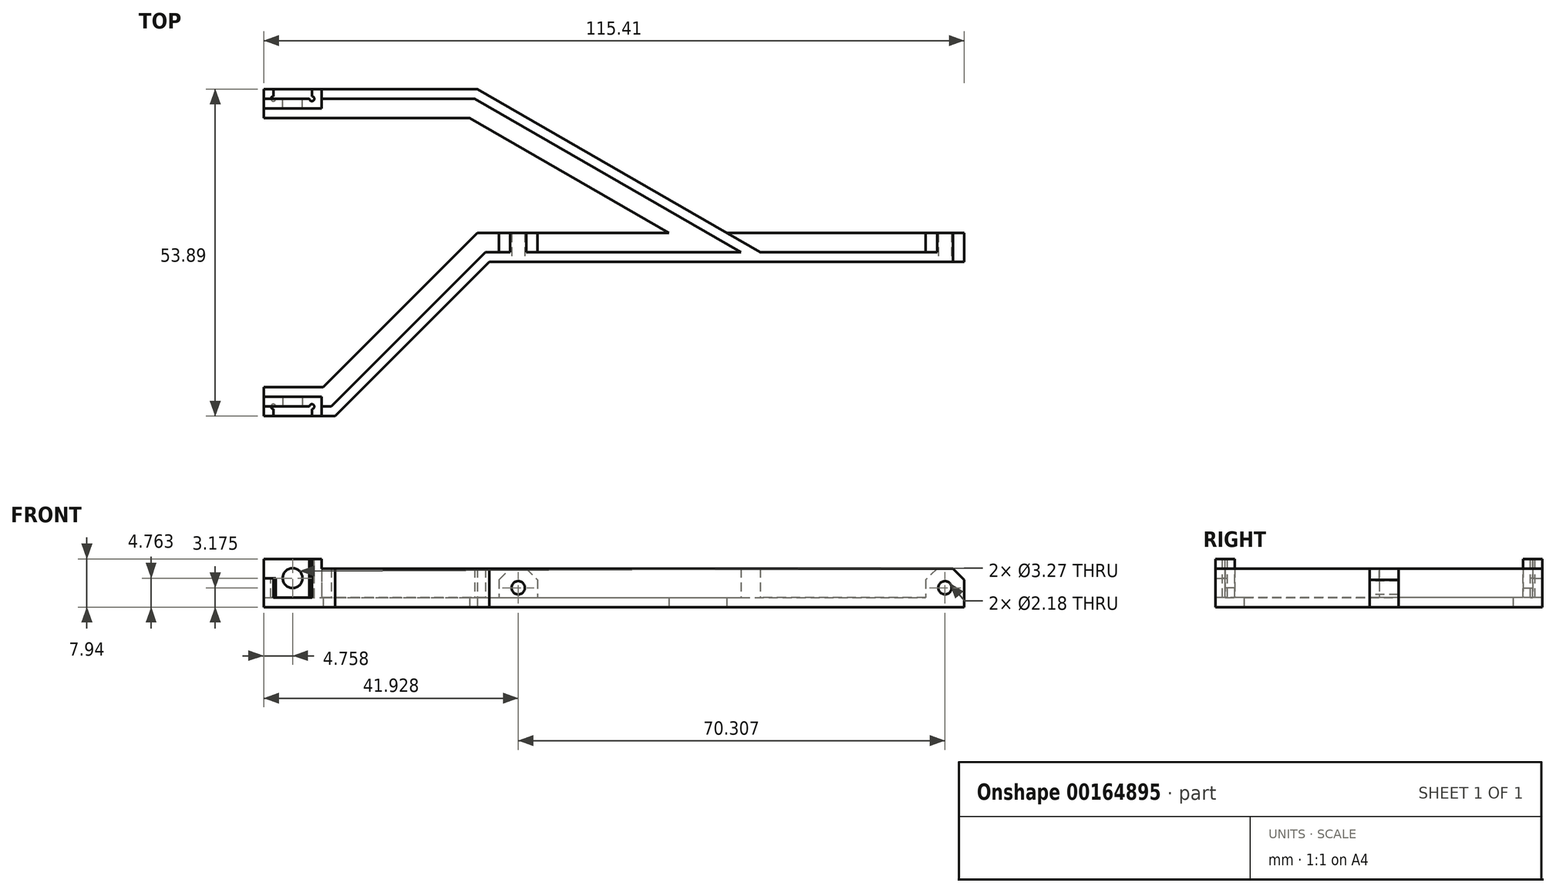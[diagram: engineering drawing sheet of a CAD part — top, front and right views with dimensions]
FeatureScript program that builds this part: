
annotation { "Feature Type Name" : "Feature", "Feature Type Description" : "" }
export const myFeature = defineFeature(function(context is Context, id is Id, definition is map)
    precondition{}
    {
        {
            var Q0;
            Q0=qCreatedBy(makeId("Top.planeOp"),FACE);
            var sketch = newSketch(context, id + "F0", { "sketchPlane" : qUnion([Q0])});
            skLineSegment(sketch, "E0", {"start": v(-127, 25.4) * mm, "end": v(-87.88, 25.4) * mm});
            skLineSegment(sketch, "E1", {"start": v(-46.78, 25.4) * mm, "end": v(-21.38, 0) * mm});
            skLineSegment(sketch, "E2", {"start": v(-21.38, 0) * mm, "end": v(21.38, 0) * mm});
            skLineSegment(sketch, "E3", {"start": v(21.38, 0) * mm, "end": v(46.78, 25.4) * mm});
            skLineSegment(sketch, "E4", {"start": v(87.88, 25.4) * mm, "end": v(127, 25.4) * mm});
            skLineSegment(sketch, "E5", {"start": v(-127, 25.4) * mm, "end": v(-127, 20.64) * mm});
            skLineSegment(sketch, "E6", {"start": v(-127, 20.64) * mm, "end": v(-48.76, 20.64) * mm});
            skLineSegment(sketch, "E7", {"start": v(-48.76, 20.64) * mm, "end": v(-23.36, -4.76) * mm});
            skLineSegment(sketch, "E8", {"start": v(-23.36, -4.76) * mm, "end": v(23.36, -4.76) * mm});
            skLineSegment(sketch, "E9", {"start": v(23.36, -4.76) * mm, "end": v(48.76, 20.64) * mm});
            skLineSegment(sketch, "E10", {"start": v(48.76, 20.64) * mm, "end": v(127, 20.64) * mm});
            skLineSegment(sketch, "E11", {"start": v(127, 20.64) * mm, "end": v(127, 25.4) * mm});
            skLineSegment(sketch, "E12", {"start": v(-34.08, 12.7) * mm, "end": v(-37.45, 9.33) * mm, "construction": true});
            skLineSegment(sketch, "E13", {"start": v(0, 0) * mm, "end": v(0, -4.76) * mm, "construction": true});
            skLineSegment(sketch, "E14", {"start": v(34.08, 12.7) * mm, "end": v(37.45, 9.33) * mm, "construction": true});
            skLineSegment(sketch, "E15", {"start": v(-87.88, 20.64) * mm, "end": v(-87.88, 25.4) * mm, "construction": true});
            skLineSegment(sketch, "E16", {"start": v(87.88, 20.64) * mm, "end": v(87.88, 25.4) * mm, "construction": true});
            skLineSegment(sketch, "E17", {"start": v(-87.88, 25.4) * mm, "end": v(-46.78, 49.13) * mm});
            skLineSegment(sketch, "E18", {"start": v(-78.35, 25.4) * mm, "end": v(-45.5, 44.36) * mm});
            skLineSegment(sketch, "E19", {"start": v(-45.5, 44.36) * mm, "end": v(45.5, 44.36) * mm});
            skLineSegment(sketch, "E20", {"start": v(-46.78, 49.13) * mm, "end": v(46.78, 49.13) * mm});
            skLineSegment(sketch, "E21", {"start": v(-78.35, 25.4) * mm, "end": v(-46.78, 25.4) * mm});
            skLineSegment(sketch, "E22", {"start": v(45.5, 44.36) * mm, "end": v(78.35, 25.4) * mm});
            skLineSegment(sketch, "E23", {"start": v(46.78, 49.13) * mm, "end": v(87.88, 25.4) * mm});
            skLineSegment(sketch, "E24", {"start": v(46.78, 25.4) * mm, "end": v(78.35, 25.4) * mm});
            skLineSegment(sketch, "E25", {"start": v(0, 0) * mm, "end": v(0, 44.36) * mm, "construction": true});
            skLineSegment(sketch, "E26", {"start": v(0, 44.36) * mm, "end": v(0, 49.13) * mm, "construction": true});
            skLineSegment(sketch, "E27", {"start": v(-61.93, 34.88) * mm, "end": v(-64.31, 39) * mm, "construction": true});
            skLineSegment(sketch, "E28", {"start": v(61.93, 34.88) * mm, "end": v(64.31, 39) * mm, "construction": true});
            skLineSegment(sketch, "E29", {"start": v(-46.78, 25.4) * mm, "end": v(0, 25.4) * mm, "construction": true});
            skLineSegment(sketch, "E30", {"start": v(0, 25.4) * mm, "end": v(46.78, 25.4) * mm, "construction": true});
            skSolve(sketch);
        }
        {
            var Q0;
            Q0=qSketchRegion(id+"F0",true);
            extrude(context, id + "F1", {"entities" : qUnion([Q0]), "depth" : 1.59 * mm});
        }
        {
            var Q0;
            Q0=makeQuery(id+"F1.opExtrude","CAP_FACE",FACE,{"disambiguationData":[OSD([sQuery(id+"F0.wireOp",EDGE,"E0"),sQuery(id+"F0.wireOp",EDGE,"E1"),sQuery(id+"F0.wireOp",EDGE,"E2"),sQuery(id+"F0.wireOp",EDGE,"E3"),sQuery(id+"F0.wireOp",EDGE,"E4"),sQuery(id+"F0.wireOp",EDGE,"E5"),sQuery(id+"F0.wireOp",EDGE,"E6"),sQuery(id+"F0.wireOp",EDGE,"E7"),sQuery(id+"F0.wireOp",EDGE,"E8"),sQuery(id+"F0.wireOp",EDGE,"E9"),sQuery(id+"F0.wireOp",EDGE,"E10"),sQuery(id+"F0.wireOp",EDGE,"E11")])],"isStart":false});
            var sketch = newSketch(context, id + "F2", { "sketchPlane" : qUnion([Q0])});
            skLineSegment(sketch, "E31.bottom", {"start": v(-127, 20.64) * mm, "end": v(-48.76, 20.64) * mm});
            skLineSegment(sketch, "E31.top", {"start": v(-127, 22.22) * mm, "end": v(-93.38, 22.22) * mm});
            skLineSegment(sketch, "E31.left", {"start": v(-127, 20.64) * mm, "end": v(-127, 22.22) * mm});
            skLineSegment(sketch, "E32", {"start": v(-48.76, 20.64) * mm, "end": v(-23.36, -4.76) * mm});
            skLineSegment(sketch, "E33", {"start": v(-23.36, -4.76) * mm, "end": v(23.36, -4.76) * mm});
            skLineSegment(sketch, "E34", {"start": v(23.36, -4.76) * mm, "end": v(48.76, 20.64) * mm});
            skLineSegment(sketch, "E35", {"start": v(48.76, 20.64) * mm, "end": v(127, 20.64) * mm});
            skLineSegment(sketch, "E36", {"start": v(127, 20.64) * mm, "end": v(127, 22.22) * mm});
            skLineSegment(sketch, "E37", {"start": v(127, 22.22) * mm, "end": v(93.38, 22.22) * mm});
            skLineSegment(sketch, "E38", {"start": v(48.1, 22.22) * mm, "end": v(22.7, -3.17) * mm});
            skLineSegment(sketch, "E39", {"start": v(-22.7, -3.18) * mm, "end": v(-48.1, 22.22) * mm});
            skLineSegment(sketch, "E40", {"start": v(-36.06, 7.94) * mm, "end": v(-34.93, 9.06) * mm, "construction": true});
            skLineSegment(sketch, "E41", {"start": v(36.06, 7.94) * mm, "end": v(34.93, 9.06) * mm, "construction": true});
            skLineSegment(sketch, "E42", {"start": v(0, -3.18) * mm, "end": v(0, -4.76) * mm, "construction": true});
            skLineSegment(sketch, "E43", {"start": v(-22.7, -3.18) * mm, "end": v(-21.11, -3.18) * mm});
            skLineSegment(sketch, "E44", {"start": v(22.7, -3.18) * mm, "end": v(21.11, -3.18) * mm});
            skLineSegment(sketch, "E45.bottom", {"start": v(-21.11, -3.18) * mm, "end": v(21.11, -3.18) * mm, "construction": true});
            skLineSegment(sketch, "E45.top", {"start": v(-21.11, -1.59) * mm, "end": v(21.11, -1.59) * mm});
            skLineSegment(sketch, "E45.left", {"start": v(-21.11, -3.18) * mm, "end": v(-21.11, -1.59) * mm});
            skLineSegment(sketch, "E45.right", {"start": v(21.11, -3.18) * mm, "end": v(21.11, -1.59) * mm});
            skLineSegment(sketch, "E46", {"start": v(-46.78, 49.13) * mm, "end": v(-93.38, 22.22) * mm});
            skLineSegment(sketch, "E47", {"start": v(-46.78, 49.13) * mm, "end": v(46.78, 49.13) * mm});
            skLineSegment(sketch, "E48", {"start": v(46.78, 49.13) * mm, "end": v(93.38, 22.22) * mm});
            skLineSegment(sketch, "E49", {"start": v(-67.33, 37.26) * mm, "end": v(-66.54, 35.89) * mm, "construction": true});
            skLineSegment(sketch, "E50", {"start": v(0, 49.13) * mm, "end": v(0, 47.54) * mm, "construction": true});
            skLineSegment(sketch, "E51", {"start": v(67.33, 37.26) * mm, "end": v(66.54, 35.89) * mm, "construction": true});
            skLineSegment(sketch, "E52", {"start": v(-90.2, 22.22) * mm, "end": v(-46.36, 47.54) * mm});
            skLineSegment(sketch, "E53", {"start": v(46.36, 47.54) * mm, "end": v(90.2, 22.23) * mm});
            skLineSegment(sketch, "E54", {"start": v(-48.1, 22.22) * mm, "end": v(-90.2, 22.22) * mm});
            skLineSegment(sketch, "E55", {"start": v(48.1, 22.22) * mm, "end": v(90.2, 22.22) * mm});
            skLineSegment(sketch, "E56.bottom", {"start": v(-21.11, 47.54) * mm, "end": v(21.11, 47.54) * mm, "construction": true});
            skLineSegment(sketch, "E56.top", {"start": v(-21.11, 45.95) * mm, "end": v(21.11, 45.95) * mm});
            skLineSegment(sketch, "E56.left", {"start": v(-21.11, 47.54) * mm, "end": v(-21.11, 45.95) * mm});
            skLineSegment(sketch, "E56.right", {"start": v(21.11, 47.54) * mm, "end": v(21.11, 45.95) * mm});
            skLineSegment(sketch, "E57", {"start": v(-21.11, 47.54) * mm, "end": v(-46.36, 47.54) * mm});
            skLineSegment(sketch, "E58", {"start": v(21.11, 47.54) * mm, "end": v(46.36, 47.54) * mm});
            skSolve(sketch);
        }
        {
            var Q0;
            Q0=makeQuery(id+"F2.imprint","IMPRINT",FACE,{"disambiguationData":[TD([[makeQuery(id+"F2.imprint","IMPRINT",EDGE,{"derivedFrom":sQuery(id+"F2.wireOp",EDGE,"E31.bottom")}),1.0]])]});
            extrude(context, id + "F3", {"entities" : qUnion([Q0]), "operationType" : NewBodyOperationType.ADD, "depth" : 4.76 * mm});
        }
        {
            var Q0;
            Q0=makeQuery(id+"F3.opExtrude","SWEPT_FACE",FACE,{"disambiguationData":[OSD([sQuery(id+"F2.wireOp",EDGE,"E31.top")])]});
            var sketch = newSketch(context, id + "F4", { "sketchPlane" : qUnion([Q0])});
            skLineSegment(sketch, "E59.bottom", {"start": v(-50.34, 6.35) * mm, "end": v(-56.7, 6.35) * mm});
            skLineSegment(sketch, "E59.top", {"start": v(-50.34, 0) * mm, "end": v(-56.7, 0) * mm});
            skLineSegment(sketch, "E59.left", {"start": v(-50.34, 6.35) * mm, "end": v(-50.34, 0) * mm});
            skLineSegment(sketch, "E59.right", {"start": v(-56.7, 6.35) * mm, "end": v(-56.7, 0) * mm});
            skLineSegment(sketch, "E60", {"start": v(-50.34, 3.18) * mm, "end": v(-48.76, 3.18) * mm, "construction": true});
            skLineSegment(sketch, "E61.bottom", {"start": v(-127, 6.35) * mm, "end": v(-120.65, 6.35) * mm});
            skLineSegment(sketch, "E61.top", {"start": v(-127, 0) * mm, "end": v(-120.65, 0) * mm});
            skLineSegment(sketch, "E61.left", {"start": v(-127, 6.35) * mm, "end": v(-127, 0) * mm});
            skLineSegment(sketch, "E61.right", {"start": v(-120.65, 6.35) * mm, "end": v(-120.65, 0) * mm});
            skLineSegment(sketch, "E62.bottom", {"start": v(127, 6.35) * mm, "end": v(120.65, 6.35) * mm});
            skLineSegment(sketch, "E62.top", {"start": v(127, 0) * mm, "end": v(120.65, 0) * mm});
            skLineSegment(sketch, "E62.left", {"start": v(127, 6.35) * mm, "end": v(127, 0) * mm});
            skLineSegment(sketch, "E62.right", {"start": v(120.65, 6.35) * mm, "end": v(120.65, 0) * mm});
            skLineSegment(sketch, "E63.bottom", {"start": v(50.34, 6.35) * mm, "end": v(56.7, 6.35) * mm});
            skLineSegment(sketch, "E63.top", {"start": v(50.34, 0) * mm, "end": v(56.7, 0) * mm});
            skLineSegment(sketch, "E63.left", {"start": v(50.34, 6.35) * mm, "end": v(50.34, 0) * mm});
            skLineSegment(sketch, "E63.right", {"start": v(56.7, 6.35) * mm, "end": v(56.7, 0) * mm});
            skLineSegment(sketch, "E64", {"start": v(120.65, 3.18) * mm, "end": v(56.7, 3.18) * mm, "construction": true});
            skLineSegment(sketch, "E65", {"start": v(-56.7, 3.18) * mm, "end": v(-120.65, 3.17) * mm, "construction": true});
            skSolve(sketch);
        }
        {
            var Q0;
            Q0=qSketchRegion(id+"F4",true);
            var Q1;
            Q1=makeQuery(id+"F1.opExtrude","SWEPT_FACE",FACE,{"disambiguationData":[OSD([sQuery(id+"F0.wireOp",EDGE,"E0")])]});
            extrude(context, id + "F5", {"entities" : qUnion([Q0]), "operationType" : NewBodyOperationType.ADD, "endBound" : BoundingType.UP_TO_SURFACE, "endBoundEntityFace" : qUnion([Q1]), "depth" : 25.4 * mm});
        }
        {
            var Q0;
            Q0=makeQuery(id+"F5.boolean.opBoolean","MERGE",EDGE,{"derivedFrom":[makeQuery(id+"F3.opExtrude","CAP_EDGE",EDGE,{"disambiguationData":[OSD([sQuery(id+"F2.wireOp",EDGE,"E31.left")])],"isStart":false}),makeQuery(id+"F5.opExtrude","SWEPT_EDGE",EDGE,{"disambiguationData":[OSD([sQuery(id+"F4.wireOp",EDGE,"E62.bottom"),sQuery(id+"F4.wireOp",EDGE,"E62.left")])]})]});
            var Q1;
            Q1=makeQuery(id+"F5.opExtrude","SWEPT_EDGE",EDGE,{"disambiguationData":[OSD([sQuery(id+"F2.wireOp",EDGE,"E31.top"),sQuery(id+"F4.wireOp",EDGE,"E62.bottom"),sQuery(id+"F4.wireOp",EDGE,"E62.right")])]});
            var Q2;
            Q2=makeQuery(id+"F5.opExtrude","SWEPT_EDGE",EDGE,{"disambiguationData":[OSD([sQuery(id+"F2.wireOp",EDGE,"E31.top"),sQuery(id+"F4.wireOp",EDGE,"E63.bottom"),sQuery(id+"F4.wireOp",EDGE,"E63.right")])]});
            var Q3;
            Q3=makeQuery(id+"F5.opExtrude","SWEPT_EDGE",EDGE,{"disambiguationData":[OSD([sQuery(id+"F2.wireOp",EDGE,"E31.top"),sQuery(id+"F4.wireOp",EDGE,"E63.bottom"),sQuery(id+"F4.wireOp",EDGE,"E63.left")])]});
            var Q4;
            Q4=makeQuery(id+"F5.opExtrude","SWEPT_EDGE",EDGE,{"disambiguationData":[OSD([sQuery(id+"F4.wireOp",EDGE,"E59.bottom"),sQuery(id+"F4.wireOp",EDGE,"E59.left")])]});
            var Q5;
            Q5=makeQuery(id+"F5.opExtrude","SWEPT_EDGE",EDGE,{"disambiguationData":[OSD([sQuery(id+"F4.wireOp",EDGE,"E59.bottom"),sQuery(id+"F4.wireOp",EDGE,"E59.right")])]});
            var Q6;
            Q6=makeQuery(id+"F5.opExtrude","SWEPT_EDGE",EDGE,{"disambiguationData":[OSD([sQuery(id+"F4.wireOp",EDGE,"E61.bottom"),sQuery(id+"F4.wireOp",EDGE,"E61.right")])]});
            var Q7;
            Q7=makeQuery(id+"F5.boolean.opBoolean","MERGE",EDGE,{"derivedFrom":[makeQuery(id+"F3.opExtrude","CAP_EDGE",EDGE,{"disambiguationData":[OSD([sQuery(id+"F2.wireOp",EDGE,"E36")])],"isStart":false}),makeQuery(id+"F5.opExtrude","SWEPT_EDGE",EDGE,{"disambiguationData":[OSD([sQuery(id+"F4.wireOp",EDGE,"E61.bottom"),sQuery(id+"F4.wireOp",EDGE,"E61.left")])]})]});
            chamfer(context, id + "F6", {"entities" : qUnion([Q0, Q1, Q2, Q3, Q4, Q5, Q6, Q7]), "width" : 1.86 * mm, "tangentPropagation" : true});
        }
        {
            var Q0;
            Q0=makeQuery(id+"F5.boolean.opBoolean","MERGE",FACE,{"derivedFrom":[makeQuery(id+"F3.opExtrude","CAP_FACE",FACE,{"disambiguationData":[OSD([sQuery(id+"F2.wireOp",EDGE,"E31.bottom"),sQuery(id+"F2.wireOp",EDGE,"E31.top"),sQuery(id+"F2.wireOp",EDGE,"E31.left"),sQuery(id+"F2.wireOp",EDGE,"E32"),sQuery(id+"F2.wireOp",EDGE,"E33"),sQuery(id+"F2.wireOp",EDGE,"E34"),sQuery(id+"F2.wireOp",EDGE,"E35"),sQuery(id+"F2.wireOp",EDGE,"E36"),sQuery(id+"F2.wireOp",EDGE,"E37"),sQuery(id+"F2.wireOp",EDGE,"E38"),sQuery(id+"F2.wireOp",EDGE,"E39"),sQuery(id+"F2.wireOp",EDGE,"E43"),sQuery(id+"F2.wireOp",EDGE,"E44"),sQuery(id+"F2.wireOp",EDGE,"E45.top"),sQuery(id+"F2.wireOp",EDGE,"E45.left"),sQuery(id+"F2.wireOp",EDGE,"E45.right")])],"isStart":false}),makeQuery(id+"F5.opExtrude","SWEPT_FACE",FACE,{"disambiguationData":[OSD([sQuery(id+"F4.wireOp",EDGE,"E59.bottom")])]}),makeQuery(id+"F5.opExtrude","SWEPT_FACE",FACE,{"disambiguationData":[OSD([sQuery(id+"F4.wireOp",EDGE,"E61.bottom")])]}),makeQuery(id+"F5.opExtrude","SWEPT_FACE",FACE,{"disambiguationData":[OSD([sQuery(id+"F4.wireOp",EDGE,"E62.bottom")])]}),makeQuery(id+"F5.opExtrude","SWEPT_FACE",FACE,{"disambiguationData":[OSD([sQuery(id+"F4.wireOp",EDGE,"E63.bottom")])]})]});
            var sketch = newSketch(context, id + "F7", { "sketchPlane" : qUnion([Q0])});
            skLineSegment(sketch, "E66.bottom", {"start": v(-21.11, -1.59) * mm, "end": v(21.11, -1.59) * mm});
            skLineSegment(sketch, "E66.top", {"start": v(-21.11, -4.76) * mm, "end": v(21.11, -4.76) * mm});
            skLineSegment(sketch, "E66.left", {"start": v(-21.11, -1.59) * mm, "end": v(-21.11, -4.76) * mm});
            skLineSegment(sketch, "E66.right", {"start": v(21.11, -1.59) * mm, "end": v(21.11, -4.76) * mm});
            skLineSegment(sketch, "E67.bottom", {"start": v(-21.11, 45.95) * mm, "end": v(21.11, 45.95) * mm});
            skLineSegment(sketch, "E67.top", {"start": v(-21.11, 49.13) * mm, "end": v(21.11, 49.13) * mm});
            skLineSegment(sketch, "E67.left", {"start": v(-21.11, 45.95) * mm, "end": v(-21.11, 49.13) * mm});
            skLineSegment(sketch, "E67.right", {"start": v(21.11, 45.95) * mm, "end": v(21.11, 49.13) * mm});
            skSolve(sketch);
        }
        {
            var Q0;
            Q0=qSketchRegion(id+"F7",true);
            extrude(context, id + "F8", {"entities" : qUnion([Q0]), "operationType" : NewBodyOperationType.ADD, "depth" : 1.59 * mm});
        }
        {
            var Q0;
            Q0=makeQuery(id+"F8.opExtrude","CAP_FACE",FACE,{"disambiguationData":[OSD([sQuery(id+"F7.wireOp",EDGE,"E67.bottom"),sQuery(id+"F7.wireOp",EDGE,"E67.top"),sQuery(id+"F7.wireOp",EDGE,"E67.left"),sQuery(id+"F7.wireOp",EDGE,"E67.right")])],"isStart":false});
            var sketch = newSketch(context, id + "F9", { "sketchPlane" : qUnion([Q0])});
            skLineSegment(sketch, "E68.bottom", {"start": v(13.17, -4.76) * mm, "end": v(19.52, -4.76) * mm});
            skLineSegment(sketch, "E68.top", {"start": v(13.17, -3.18) * mm, "end": v(19.52, -3.18) * mm});
            skLineSegment(sketch, "E68.left", {"start": v(13.17, -4.76) * mm, "end": v(13.17, -3.18) * mm});
            skLineSegment(sketch, "E68.right", {"start": v(19.52, -4.76) * mm, "end": v(19.52, -3.18) * mm});
            skLineSegment(sketch, "E69.bottom", {"start": v(19.52, -3.18) * mm, "end": v(21.11, -3.18) * mm, "construction": true});
            skLineSegment(sketch, "E69.top", {"start": v(19.52, -1.59) * mm, "end": v(21.11, -1.59) * mm, "construction": true});
            skLineSegment(sketch, "E69.left", {"start": v(19.52, -3.18) * mm, "end": v(19.52, -1.59) * mm, "construction": true});
            skLineSegment(sketch, "E69.right", {"start": v(21.11, -3.18) * mm, "end": v(21.11, -1.59) * mm, "construction": true});
            skLineSegment(sketch, "E70.bottom", {"start": v(21.11, 47.54) * mm, "end": v(19.52, 47.54) * mm, "construction": true});
            skLineSegment(sketch, "E70.top", {"start": v(21.11, 45.95) * mm, "end": v(19.52, 45.95) * mm, "construction": true});
            skLineSegment(sketch, "E70.left", {"start": v(21.11, 47.54) * mm, "end": v(21.11, 45.95) * mm, "construction": true});
            skLineSegment(sketch, "E70.right", {"start": v(19.52, 47.54) * mm, "end": v(19.52, 45.95) * mm, "construction": true});
            skLineSegment(sketch, "E71.bottom", {"start": v(13.17, 47.54) * mm, "end": v(19.52, 47.54) * mm});
            skLineSegment(sketch, "E71.top", {"start": v(13.17, 49.13) * mm, "end": v(19.52, 49.13) * mm});
            skLineSegment(sketch, "E71.left", {"start": v(13.17, 47.54) * mm, "end": v(13.17, 49.13) * mm});
            skLineSegment(sketch, "E71.right", {"start": v(19.52, 47.54) * mm, "end": v(19.52, 49.13) * mm});
            skSolve(sketch);
        }
        {
            var Q0;
            Q0=qSketchRegion(id+"F9",true);
            var Q1;
            {var subQ3=sQuery(id+"F0.wireOp",EDGE,"E21");var subQ6=sQuery(id+"F0.wireOp",EDGE,"E24");var subQ9=sQuery(id+"F0.wireOp",EDGE,"E1");var subQ10=makeQuery(id+"F1.opExtrude","SWEPT_FACE",FACE,{"disambiguationData":[OSD([subQ9])]});var subQ13=sQuery(id+"F0.wireOp",EDGE,"E2");var subQ16=sQuery(id+"F0.wireOp",EDGE,"E3");var subQ18=sQuery(id+"F0.wireOp",EDGE,"E0");var subQ22=sQuery(id+"F0.wireOp",EDGE,"E18");var subQ23=sQuery(id+"F0.wireOp",EDGE,"E19");var subQ24=sQuery(id+"F0.wireOp",EDGE,"E22");Q1=makeQuery(id+"F5.boolean.opBoolean","SPLIT",FACE,{"disambiguationData":[TD([subQ10])],"derivedFrom":makeQuery(id+"F3.boolean.opBoolean","SPLIT",FACE,{"disambiguationData":[TD([subQ10])],"derivedFrom":makeQuery(id+"F1.opExtrude","CAP_FACE",FACE,{"disambiguationData":[OSD([subQ18,subQ9,subQ13,subQ16,sQuery(id+"F0.wireOp",EDGE,"E4"),sQuery(id+"F0.wireOp",EDGE,"E5"),sQuery(id+"F0.wireOp",EDGE,"E6"),sQuery(id+"F0.wireOp",EDGE,"E7"),sQuery(id+"F0.wireOp",EDGE,"E8"),sQuery(id+"F0.wireOp",EDGE,"E9"),sQuery(id+"F0.wireOp",EDGE,"E10"),sQuery(id+"F0.wireOp",EDGE,"E11"),sQuery(id+"F0.wireOp",EDGE,"E17"),subQ22,subQ23,sQuery(id+"F0.wireOp",EDGE,"E20"),subQ3,subQ24,sQuery(id+"F0.wireOp",EDGE,"E23"),subQ6])],"isStart":false})})});}
            extrude(context, id + "F10", {"entities" : qUnion([Q0]), "operationType" : NewBodyOperationType.REMOVE, "endBound" : BoundingType.UP_TO_SURFACE, "oppositeDirection" : true, "endBoundEntityFace" : qUnion([Q1]), "depth" : 25.4 * mm});
        }
        {
            var Q0;
            Q0=makeQuery(id+"F10.boolean.opBoolean","COPY",FACE,{"derivedFrom":makeQuery(id+"F10.opExtrude","SWEPT_FACE",FACE,{"disambiguationData":[OSD([sQuery(id+"F9.wireOp",EDGE,"E68.top")])]})});
            var sketch = newSketch(context, id + "F11", { "sketchPlane" : qUnion([Q0])});
            skLineSegment(sketch, "E72", {"start": v(123.82, 6.35) * mm, "end": v(123.82, 0) * mm, "construction": true});
            skLineSegment(sketch, "E73", {"start": v(53.52, 6.35) * mm, "end": v(53.52, 0) * mm, "construction": true});
            skCircle(sketch, "E74", {"center": v(53.52, 3.17) * mm, "radius": 1.1 * mm});
            skCircle(sketch, "E75", {"center": v(123.82, 3.18) * mm, "radius": 1.1 * mm});
            skLineSegment(sketch, "E76", {"start": v(-53.52, 6.35) * mm, "end": v(-53.52, 0) * mm, "construction": true});
            skLineSegment(sketch, "E77", {"start": v(-123.82, 6.35) * mm, "end": v(-123.82, 0) * mm, "construction": true});
            skCircle(sketch, "E78", {"center": v(-123.82, 3.18) * mm, "radius": 1.1 * mm});
            skCircle(sketch, "E79", {"center": v(-53.52, 3.18) * mm, "radius": 1.1 * mm});
            skLineSegment(sketch, "E80", {"start": v(16.35, 7.94) * mm, "end": v(16.35, 4.76) * mm, "construction": true});
            skCircle(sketch, "E81", {"center": v(16.35, 4.76) * mm, "radius": 1.63 * mm});
            skSolve(sketch);
        }
        {
            var Q0;
            Q0=qSketchRegion(id+"F11",true);
            var Q1;
            Q1=makeQuery(id+"F5.boolean.opBoolean","MERGE",FACE,{"derivedFrom":[makeQuery(id+"F1.opExtrude","SWEPT_FACE",FACE,{"disambiguationData":[OSD([sQuery(id+"F0.wireOp",EDGE,"E21")])]}),makeQuery(id+"F5.opExtrude","CAP_FACE",FACE,{"disambiguationData":[OSD([sQuery(id+"F0.wireOp",EDGE,"E0")]),ownerDisambiguation([makeQuery(id+"F5.opExtrude","SWEPT_BODY",BODY,{"disambiguationData":[OSD([sQuery(id+"F4.wireOp",EDGE,"E63.bottom"),sQuery(id+"F4.wireOp",EDGE,"E63.top"),sQuery(id+"F4.wireOp",EDGE,"E63.left"),sQuery(id+"F4.wireOp",EDGE,"E63.right")])]})])],"isStart":false})]});
            extrude(context, id + "F12", {"entities" : qUnion([Q0]), "operationType" : NewBodyOperationType.REMOVE, "endBound" : BoundingType.UP_TO_SURFACE, "oppositeDirection" : true, "endBoundEntityFace" : qUnion([Q1]), "depth" : 25.4 * mm});
        }
        {
            var Q0;
            Q0=makeQuery(id+"F8.opExtrude","CAP_EDGE",EDGE,{"disambiguationData":[OSD([sQuery(id+"F7.wireOp",EDGE,"E66.left")])],"isStart":true});
            var Q1;
            Q1=makeQuery(id+"F8.opExtrude","CAP_EDGE",EDGE,{"disambiguationData":[OSD([sQuery(id+"F7.wireOp",EDGE,"E66.right")])],"isStart":true});
            var Q2;
            Q2=makeQuery(id+"F8.opExtrude","CAP_EDGE",EDGE,{"disambiguationData":[OSD([sQuery(id+"F7.wireOp",EDGE,"E67.left")])],"isStart":true});
            var Q3;
            Q3=makeQuery(id+"F8.opExtrude","CAP_EDGE",EDGE,{"disambiguationData":[OSD([sQuery(id+"F7.wireOp",EDGE,"E67.right")])],"isStart":true});
            chamfer(context, id + "F13", {"entities" : qUnion([Q0, Q1, Q2, Q3]), "width" : 1.59 * mm, "tangentPropagation" : true});
        }
        {
            var Q0;
            Q0=makeQuery(id+"F8.opExtrude","CAP_FACE",FACE,{"disambiguationData":[OSD([sQuery(id+"F7.wireOp",EDGE,"E67.bottom"),sQuery(id+"F7.wireOp",EDGE,"E67.top"),sQuery(id+"F7.wireOp",EDGE,"E67.left"),sQuery(id+"F7.wireOp",EDGE,"E67.right")])],"isStart":false});
            var sketch = newSketch(context, id + "F14", { "sketchPlane" : qUnion([Q0])});
            skCircle(sketch, "E82", {"center": v(19.52, -3.18) * mm, "radius": 0.4 * mm});
            skCircle(sketch, "E83", {"center": v(19.52, 47.54) * mm, "radius": 0.4 * mm});
            skSolve(sketch);
        }
        {
            var Q0;
            Q0=qSketchRegion(id+"F14",true);
            var Q1;
            Q1=makeQuery(id+"F10.boolean.opBoolean","COPY",FACE,{"derivedFrom":makeQuery(id+"F10.opExtrude","CAP_FACE",FACE,{"disambiguationData":[OSD([sQuery(id+"F9.wireOp",EDGE,"E68.bottom"),sQuery(id+"F9.wireOp",EDGE,"E68.top"),sQuery(id+"F9.wireOp",EDGE,"E68.left"),sQuery(id+"F9.wireOp",EDGE,"E68.right")])],"isStart":false})});
            extrude(context, id + "F15", {"entities" : qUnion([Q0]), "operationType" : NewBodyOperationType.REMOVE, "endBound" : BoundingType.UP_TO_SURFACE, "oppositeDirection" : true, "endBoundEntityFace" : qUnion([Q1]), "depth" : 25.4 * mm});
        }
        {
            var Q0;
            Q0=makeQuery(id+"F10.boolean.opBoolean","COPY",FACE,{"derivedFrom":makeQuery(id+"F10.opExtrude","SWEPT_FACE",FACE,{"disambiguationData":[OSD([sQuery(id+"F9.wireOp",EDGE,"E71.bottom")])]})});
            var sketch = newSketch(context, id + "F16", { "sketchPlane" : qUnion([Q0])});
            skCircle(sketch, "E84", {"center": v(-16.35, 4.76) * mm, "radius": 1.63 * mm});
            skSolve(sketch);
        }
        {
            var Q0;
            Q0=qSketchRegion(id+"F16",true);
            var Q1;
            Q1=makeQuery(id+"F8.boolean.opBoolean","MERGE",FACE,{"derivedFrom":[makeQuery(id+"F3.opExtrude","SWEPT_FACE",FACE,{"disambiguationData":[OSD([sQuery(id+"F2.wireOp",EDGE,"E56.top")])]}),makeQuery(id+"F8.opExtrude","SWEPT_FACE",FACE,{"disambiguationData":[OSD([sQuery(id+"F7.wireOp",EDGE,"E67.bottom")])]})]});
            extrude(context, id + "F17", {"entities" : qUnion([Q0]), "operationType" : NewBodyOperationType.REMOVE, "endBound" : BoundingType.UP_TO_SURFACE, "oppositeDirection" : true, "endBoundEntityFace" : qUnion([Q1]), "depth" : 25.4 * mm});
        }
        {
            var Q0;
            Q0=makeQuery(id+"F8.opExtrude","CAP_FACE",FACE,{"disambiguationData":[OSD([sQuery(id+"F7.wireOp",EDGE,"E67.bottom"),sQuery(id+"F7.wireOp",EDGE,"E67.top"),sQuery(id+"F7.wireOp",EDGE,"E67.left"),sQuery(id+"F7.wireOp",EDGE,"E67.right")])],"isStart":false});
            var sketch = newSketch(context, id + "F18", { "sketchPlane" : qUnion([Q0])});
            skLineSegment(sketch, "E85.bottom", {"start": v(11.59, 49.13) * mm, "end": v(-127, 49.13) * mm});
            skLineSegment(sketch, "E85.top", {"start": v(11.59, -4.76) * mm, "end": v(-127, -4.76) * mm});
            skLineSegment(sketch, "E85.left", {"start": v(11.59, 49.13) * mm, "end": v(11.59, -4.76) * mm});
            skLineSegment(sketch, "E85.right", {"start": v(-127, 49.13) * mm, "end": v(-127, -4.76) * mm});
            skLineSegment(sketch, "E86", {"start": v(13.17, -3.97) * mm, "end": v(11.59, -3.97) * mm, "construction": true});
            skSolve(sketch);
        }
        {
            var Q0;
            Q0 = qSketchRegion(id + "F18", true);
            var Q1;
            Q1=makeQuery(id+"F1.opExtrude","CAP_FACE",FACE,{"disambiguationData":[OSD([sQuery(id+"F0.wireOp",EDGE,"E0"),sQuery(id+"F0.wireOp",EDGE,"E1"),sQuery(id+"F0.wireOp",EDGE,"E2"),sQuery(id+"F0.wireOp",EDGE,"E3"),sQuery(id+"F0.wireOp",EDGE,"E4"),sQuery(id+"F0.wireOp",EDGE,"E5"),sQuery(id+"F0.wireOp",EDGE,"E6"),sQuery(id+"F0.wireOp",EDGE,"E7"),sQuery(id+"F0.wireOp",EDGE,"E8"),sQuery(id+"F0.wireOp",EDGE,"E9"),sQuery(id+"F0.wireOp",EDGE,"E10"),sQuery(id+"F0.wireOp",EDGE,"E11"),sQuery(id+"F0.wireOp",EDGE,"E17"),sQuery(id+"F0.wireOp",EDGE,"E18"),sQuery(id+"F0.wireOp",EDGE,"E19"),sQuery(id+"F0.wireOp",EDGE,"E20"),sQuery(id+"F0.wireOp",EDGE,"E21"),sQuery(id+"F0.wireOp",EDGE,"E22"),sQuery(id+"F0.wireOp",EDGE,"E23"),sQuery(id+"F0.wireOp",EDGE,"E24")])],"isStart":true});
            extrude(context, id + "F19", {"entities" : qUnion([Q0]), "operationType" : NewBodyOperationType.REMOVE, "endBound" : BoundingType.UP_TO_SURFACE, "oppositeDirection" : true, "endBoundEntityFace" : qUnion([Q1]), "depth" : 25.4 * mm});
        }
        {
            var Q0;
            Q0=makeQuery(id+"F10.boolean.opBoolean","COPY",FACE,{"derivedFrom":makeQuery(id+"F10.opExtrude","SWEPT_FACE",FACE,{"disambiguationData":[OSD([sQuery(id+"F9.wireOp",EDGE,"E68.left")])]})});
            var sketch = newSketch(context, id + "F20", { "sketchPlane" : qUnion([Q0])});
            skLineSegment(sketch, "E87.bottom", {"start": v(47.54, 7.94) * mm, "end": v(49.13, 7.94) * mm});
            skLineSegment(sketch, "E87.top", {"start": v(47.54, 4.76) * mm, "end": v(49.13, 4.76) * mm});
            skLineSegment(sketch, "E87.left", {"start": v(47.54, 7.94) * mm, "end": v(47.54, 4.76) * mm});
            skLineSegment(sketch, "E87.right", {"start": v(49.13, 7.94) * mm, "end": v(49.13, 4.76) * mm});
            skLineSegment(sketch, "E88.bottom", {"start": v(-4.76, 4.76) * mm, "end": v(-3.18, 4.76) * mm});
            skLineSegment(sketch, "E88.top", {"start": v(-4.76, 7.94) * mm, "end": v(-3.18, 7.94) * mm});
            skLineSegment(sketch, "E88.left", {"start": v(-4.76, 4.76) * mm, "end": v(-4.76, 7.94) * mm});
            skLineSegment(sketch, "E88.right", {"start": v(-3.18, 4.76) * mm, "end": v(-3.18, 7.94) * mm});
            skSolve(sketch);
        }
        {
            var Q0;
            Q0 = qSketchRegion(id + "F20", true);
            var Q1;
            {var subQ1=sQuery(id+"F0.wireOp",EDGE,"E2");Q1=makeQuery(id+"F19.boolean.opBoolean","COPY",FACE,{"disambiguationData":[TD([makeQuery(id+"F1.opExtrude","SWEPT_FACE",FACE,{"disambiguationData":[OSD([subQ1])]})])],"derivedFrom":makeQuery(id+"F19.opExtrude","SWEPT_FACE",FACE,{"disambiguationData":[OSD([sQuery(id+"F18.wireOp",EDGE,"E85.left")])]})});}
            extrude(context, id + "F21", {"entities" : qUnion([Q0]), "operationType" : NewBodyOperationType.REMOVE, "endBound" : BoundingType.UP_TO_SURFACE, "oppositeDirection" : true, "endBoundEntityFace" : qUnion([Q1]), "depth" : 25.4 * mm});
        }
        {
            var Q0;
            Q0=makeQuery(id+"F21.boolean.opBoolean","COPY",FACE,{"derivedFrom":makeQuery(id+"F21.opExtrude","SWEPT_FACE",FACE,{"disambiguationData":[OSD([sQuery(id+"F20.wireOp",EDGE,"E87.top")])]})});
            var sketch = newSketch(context, id + "F22", { "sketchPlane" : qUnion([Q0])});
            skCircle(sketch, "E89", {"center": v(13.17, -3.18) * mm, "radius": 0.4 * mm});
            skCircle(sketch, "E90", {"center": v(13.17, 47.54) * mm, "radius": 0.4 * mm});
            skSolve(sketch);
        }
        {
            var Q0;
            Q0 = qSketchRegion(id + "F22", true);
            var Q1;
            Q1=makeQuery(id+"F15.boolean.opBoolean","MERGE",FACE,{"derivedFrom":[makeQuery(id+"F10.boolean.opBoolean","COPY",FACE,{"derivedFrom":makeQuery(id+"F10.opExtrude","CAP_FACE",FACE,{"disambiguationData":[OSD([sQuery(id+"F9.wireOp",EDGE,"E71.bottom"),sQuery(id+"F9.wireOp",EDGE,"E71.top"),sQuery(id+"F9.wireOp",EDGE,"E71.left"),sQuery(id+"F9.wireOp",EDGE,"E71.right")])],"isStart":false})}),makeQuery(id+"F15.opExtrude","CAP_FACE",FACE,{"disambiguationData":[OSD([sQuery(id+"F9.wireOp",EDGE,"E68.bottom"),sQuery(id+"F9.wireOp",EDGE,"E68.top"),sQuery(id+"F9.wireOp",EDGE,"E68.left"),sQuery(id+"F9.wireOp",EDGE,"E68.right")]),ownerDisambiguation([makeQuery(id+"F15.opExtrude","SWEPT_BODY",BODY,{"disambiguationData":[OSD([sQuery(id+"F14.wireOp",EDGE,"E83")])]})])],"isStart":false})]});
            extrude(context, id + "F23", {"entities" : qUnion([Q0]), "operationType" : NewBodyOperationType.REMOVE, "endBound" : BoundingType.UP_TO_SURFACE, "oppositeDirection" : true, "endBoundEntityFace" : qUnion([Q1]), "depth" : 25.4 * mm});
        }
    });
